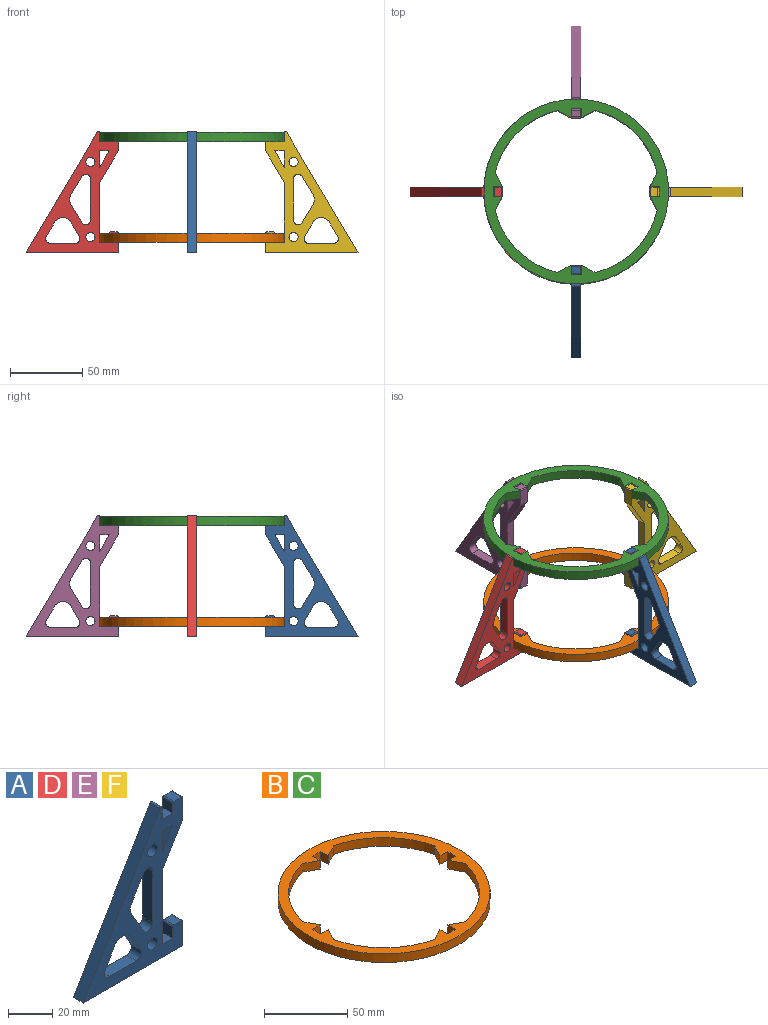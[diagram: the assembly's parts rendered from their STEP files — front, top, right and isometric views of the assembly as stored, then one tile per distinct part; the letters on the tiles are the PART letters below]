
ASSEMBLY  parts=6 mates=1
PART A: 37 faces, bbox 63.8x6.4x83.7 mm
  f0: plane 6.64x6.35mm, normal (0,0,-1), area 42.1mm2, adj f1,f34,f35,f36
  f1: plane 11.2x6.64mm, normal (-0.86,0,0.51), area 82.7mm2, adj f0,f34,f35,f36
  f2: plane 41.27x6.35mm, normal (1,0,0), area 262.1mm2, adj f3,f29,f35,f36
  f3: plane 21.81x12.92mm, normal (0.86,0,-0.51), area 160.9mm2, adj f2,f4,f35,f36
  f4: plane 11.92x6.35mm, normal (1,0,0), area 75.7mm2, adj f3,f5,f35,f36
  f5: cylinder r=0.78mm len=6.35mm, axis (0,1,0), area 7.8mm2, adj f4,f6,f35,f36
  f6: plane 6.35x4.78mm, normal (0,0,1), area 30.4mm2, adj f5,f7,f35,f36
  f7: cylinder r=0.78mm len=6.35mm, axis (0,1,0), area 7.8mm2, adj f6,f8,f35,f36
  f8: plane 6.35x5.57mm, normal (-1,0,-0.01), area 35.3mm2, adj f7,f9,f35,f36
  f9: plane 6.6x6.35mm, normal (0,0,1), area 41.9mm2, adj f8,f10,f35,f36
  f10: plane 6.35x6.32mm, normal (1,0,0), area 40.1mm2, adj f9,f11,f35,f36
  f11: cylinder r=0.78mm len=6.35mm, axis (0,1,0), area 12.9mm2, adj f10,f12,f35,f36
  f12: plane 83.27x49.35mm, normal (-0.86,0,0.51), area 614.7mm2, adj f11,f13,f35,f36
  f13: plane 63.75x6.35mm, normal (0,0,-1), area 404.8mm2, adj f12,f14,f35,f36
  f14: plane 13.48x6.35mm, normal (1,0,0), area 85.6mm2, adj f13,f15,f35,f36
  f15: cylinder r=0.78mm len=6.35mm, axis (0,1,0), area 7.8mm2, adj f14,f16,f35,f36
  f16: plane 6.35x4.79mm, normal (0,0,1), area 30.4mm2, adj f15,f17,f35,f36
  f17: cylinder r=0.78mm len=6.35mm, axis (0,1,0), area 7.8mm2, adj f16,f18,f35,f36
  f18: plane 6.35x6.35mm, normal (-1,0,0), area 40.3mm2, adj f17,f29,f35,f36
  f19: cylinder r=3.17mm len=6.35mm, axis (0,1,0), area 42.5mm2, adj f20,f30,f35,f36
  f20: plane 17.37x6.35mm, normal (0,0,1), area 110.3mm2, adj f19,f21,f35,f36
  f21: cylinder r=3.17mm len=6.35mm, axis (0,1,0), area 42.5mm2, adj f20,f22,f35,f36
  f22: plane 10.04x6.35mm, normal (0.86,0,-0.51), area 74.1mm2, adj f21,f23,f35,f36
  f23: cylinder r=6.35mm len=10.93mm, axis (0,1,0), area 83.5mm2, adj f22,f30,f35,f36
  f24: cylinder r=6.35mm len=6.47mm, axis (0,1,0), area 43.1mm2, adj f25,f31,f35,f36
  f25: plane 12.79x7.58mm, normal (0.86,0,-0.51), area 94.4mm2, adj f24,f26,f35,f36
  f26: cylinder r=3.15mm len=6.35mm, axis (0,1,0), area 52.1mm2, adj f25,f27,f35,f36
  f27: plane 28.76x6.35mm, normal (-1,0,0), area 182.6mm2, adj f26,f28,f35,f36
  f28: cylinder r=3.17mm len=6.35mm, axis (0,1,0), area 52.6mm2, adj f27,f31,f35,f36
  f29: plane 6.6x6.35mm, normal (0,0,1), area 41.9mm2, adj f2,f18,f35,f36
  f30: plane 10.04x6.35mm, normal (-0.86,0,-0.51), area 74.1mm2, adj f19,f23,f35,f36
  f31: plane 12.71x7.53mm, normal (0.86,0,0.51), area 93.8mm2, adj f24,f28,f35,f36
  f32: cylinder r=3.17mm len=6.35mm, axis (0,1,0), area 126.7mm2, adj f35,f36
  f33: cylinder r=3.17mm len=6.35mm, axis (0,1,0), area 126.7mm2, adj f35,f36
  f34: plane 11.2x6.35mm, normal (1,0,0), area 71.1mm2, adj f0,f1,f35,f36
  f35: plane 83.66x63.75mm, normal (0,-1,0), area 1824.4mm2, adj f0,f1,f2,f3,f4,f5,f6,f7
  f36: plane 83.66x63.75mm, normal (0,1,0), area 1824.4mm2, adj f0,f1,f2,f3,f4,f5,f6,f7
PART B: 27 faces, bbox 127.5x127.5x6.4 mm
  f0: cylinder r=57.4mm len=6.86mm, axis (0,0,-1), area 43.6mm2, adj f9,f10,f16,f26
  f1: cylinder r=57.4mm len=42.88mm, axis (0,0,-1), area 405.7mm2, adj f9,f10,f13,f23
  f2: cylinder r=57.4mm len=6.86mm, axis (0,0,-1), area 43.6mm2, adj f9,f10,f20,f22
  f3: cylinder r=57.4mm len=42.88mm, axis (0,0,-1), area 405.7mm2, adj f9,f10,f17,f19
  f4: cylinder r=57.4mm len=6.86mm, axis (0,0,-1), area 43.6mm2, adj f9,f10,f18,f24
  f5: cylinder r=57.4mm len=42.88mm, axis (0,0,-1), area 405.7mm2, adj f9,f10,f15,f21
  f6: cylinder r=57.4mm len=6.86mm, axis (0,0,-1), area 43.6mm2, adj f9,f10,f12,f14
  f7: cylinder r=57.4mm len=42.88mm, axis (0,0,-1), area 405.7mm2, adj f9,f10,f11,f25
  f8: cylinder r=63.75mm len=127.51mm, axis (0,0,-1), area 2543.7mm2, adj f9,f10
  f9: plane 127.51x127.51mm, normal (0,0,1), area 2672.2mm2, adj f0,f1,f2,f3,f4,f5,f6,f7
  f10: plane 127.51x127.51mm, normal (0,0,-1), area 2672.2mm2, adj f0,f1,f2,f3,f4,f5,f6,f7
  f11: plane 9.6x6.35mm, normal (0.89,-0.46,0), area 68.6mm2, adj f7,f9,f10,f12
  f12: plane 6.37x6.35mm, normal (0,1,0), area 40.4mm2, adj f6,f9,f10,f11
  f13: plane 9.6x6.35mm, normal (0.89,0.46,0), area 68.6mm2, adj f1,f9,f10,f14
  f14: plane 6.37x6.35mm, normal (0,-1,0), area 40.4mm2, adj f6,f9,f10,f13
  f15: plane 9.6x6.35mm, normal (0.46,0.89,0), area 68.6mm2, adj f5,f9,f10,f16
  f16: plane 6.37x6.35mm, normal (-1,0,0), area 40.4mm2, adj f0,f9,f10,f15
  f17: plane 9.6x6.35mm, normal (0.46,-0.89,0), area 68.6mm2, adj f3,f9,f10,f18
  f18: plane 6.37x6.35mm, normal (-1,0,0), area 40.4mm2, adj f4,f9,f10,f17
  f19: plane 9.6x6.35mm, normal (-0.89,0.46,0), area 68.6mm2, adj f3,f9,f10,f20
  f20: plane 6.37x6.35mm, normal (0,-1,0), area 40.4mm2, adj f2,f9,f10,f19
  f21: plane 9.6x6.35mm, normal (-0.89,-0.46,0), area 68.6mm2, adj f5,f9,f10,f22
  f22: plane 6.37x6.35mm, normal (0,1,0), area 40.4mm2, adj f2,f9,f10,f21
  f23: plane 9.6x6.35mm, normal (-0.46,-0.89,0), area 68.6mm2, adj f1,f9,f10,f24
  f24: plane 6.37x6.35mm, normal (1,0,0), area 40.4mm2, adj f4,f9,f10,f23
  f25: plane 9.6x6.35mm, normal (-0.46,0.89,0), area 68.6mm2, adj f7,f9,f10,f26
  f26: plane 6.37x6.35mm, normal (1,0,0), area 40.4mm2, adj f0,f9,f10,f25
PART C: same geometry as B
PART D: same geometry as A
PART E: same geometry as A
PART F: same geometry as A
PLACE A rot(axis=(0,0,1),90deg) t=(0,0,0)mm
PLACE B at identity
PLACE C t=(0.15,0.25,69.42)mm
PLACE D at identity
PLACE E rot(axis=(0,0,-1),90deg) t=(0,0,0)mm
PLACE F rot(axis=(0,0,1),180deg) t=(0,0,0)mm
MATE planar C.f10 <-> D.f9  axis (0,0,-1) through (-57.15,-3.18,76.56)mm
